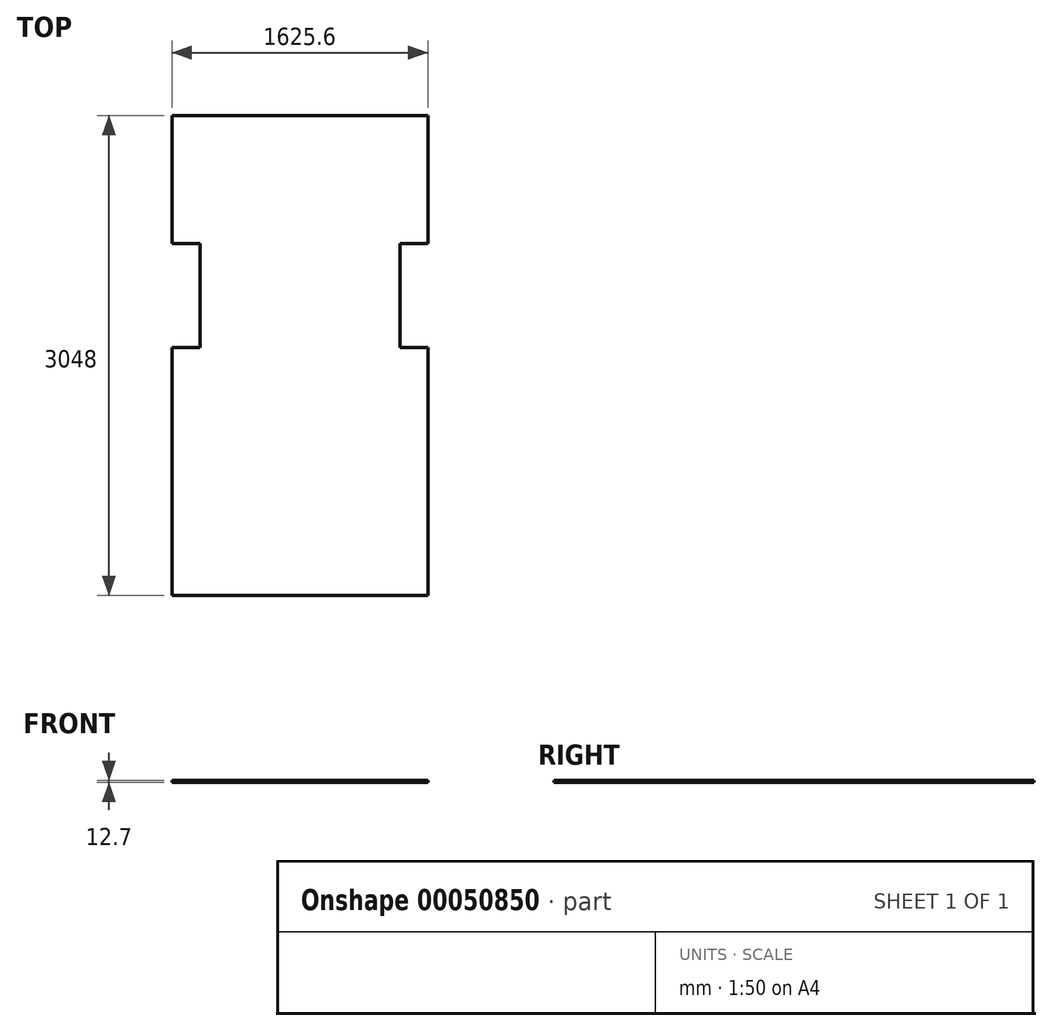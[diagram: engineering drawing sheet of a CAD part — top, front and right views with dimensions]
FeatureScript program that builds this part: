
annotation { "Feature Type Name" : "Feature", "Feature Type Description" : "" }
export const myFeature = defineFeature(function(context is Context, id is Id, definition is map)
    precondition{}
    {
        {
            var Q0;
            Q0=qCreatedBy(makeId("Top.planeOp"),FACE);
            var sketch = newSketch(context, id + "F0", { "sketchPlane" : qUnion([Q0])});
            skLineSegment(sketch, "E0.rect.bottom", {"start": v(812.8, 1524) * mm, "end": v(-812.8, 1524) * mm});
            skLineSegment(sketch, "E0.rect.top", {"start": v(812.8, -1524) * mm, "end": v(-812.8, -1524) * mm});
            skLineSegment(sketch, "E0.rect.left", {"start": v(812.8, 1524) * mm, "end": v(812.8, -1524) * mm});
            skLineSegment(sketch, "E0.rect.right", {"start": v(-812.8, 1524) * mm, "end": v(-812.8, -1524) * mm});
            skPoint(sketch, "E0.rect.middle", {"position": v(0, 0) * mm});
            skSolve(sketch);
        }
        {
            var Q0;
            Q0=makeQuery(id+"F0.imprint","IMPRINT",FACE,{"disambiguationData":[TD([[makeQuery(id+"F0.imprint","IMPRINT",EDGE,{"derivedFrom":sQuery(id+"F0.wireOp",EDGE,"E0.rect.bottom")}),1.0]])]});
            extrude(context, id + "F1", {"entities" : qUnion([Q0]), "depth" : 12.7 * mm});
        }
        {
            var Q0;
            Q0=makeQuery(id+"F1.opExtrude","CAP_FACE",FACE,{"disambiguationData":[OSD([sQuery(id+"F0.wireOp",EDGE,"E0.rect.bottom"),sQuery(id+"F0.wireOp",EDGE,"E0.rect.top"),sQuery(id+"F0.wireOp",EDGE,"E0.rect.left"),sQuery(id+"F0.wireOp",EDGE,"E0.rect.right")])],"isStart":false});
            var sketch = newSketch(context, id + "F2", { "sketchPlane" : qUnion([Q0])});
            skLineSegment(sketch, "E1", {"start": v(0, -1524) * mm, "end": v(0, 1524) * mm, "construction": true});
            skLineSegment(sketch, "E2", {"start": v(812.8, 0) * mm, "end": v(-812.8, 0) * mm, "construction": true});
            skLineSegment(sketch, "E3.bottom", {"start": v(812.8, 50.8) * mm, "end": v(635, 50.8) * mm});
            skLineSegment(sketch, "E3.top", {"start": v(812.8, 711.2) * mm, "end": v(635, 711.2) * mm});
            skLineSegment(sketch, "E3.left", {"start": v(812.8, 50.8) * mm, "end": v(812.8, 711.2) * mm});
            skLineSegment(sketch, "E3.right", {"start": v(635, 50.8) * mm, "end": v(635, 711.2) * mm});
            skLineSegment(sketch, "E4.MirrorCS", {"start": v(-812.8, 50.8) * mm, "end": v(-635, 50.8) * mm});
            skLineSegment(sketch, "E5.MirrorCS", {"start": v(-812.8, 50.8) * mm, "end": v(-812.8, 711.2) * mm});
            skLineSegment(sketch, "E6.MirrorCS", {"start": v(-635, 50.8) * mm, "end": v(-635, 711.2) * mm});
            skLineSegment(sketch, "E7.MirrorCS", {"start": v(-812.8, 711.2) * mm, "end": v(-635, 711.2) * mm});
            skSolve(sketch);
        }
        {
            var Q0;
            Q0=makeQuery(id+"F2.imprint","IMPRINT",FACE,{"disambiguationData":[TD([[makeQuery(id+"F2.imprint","IMPRINT",EDGE,{"derivedFrom":sQuery(id+"F2.wireOp",EDGE,"E4.MirrorCS")}),1.0]])]});
            var Q1;
            Q1=makeQuery(id+"F2.imprint","IMPRINT",FACE,{"disambiguationData":[TD([[makeQuery(id+"F2.imprint","IMPRINT",EDGE,{"derivedFrom":sQuery(id+"F2.wireOp",EDGE,"E3.bottom")}),-1.0]])]});
            extrude(context, id + "F3", {"entities" : qUnion([Q0, Q1]), "operationType" : NewBodyOperationType.REMOVE, "endBound" : BoundingType.THROUGH_ALL, "oppositeDirection" : true, "depth" : 25.4 * mm});
        }
    });
